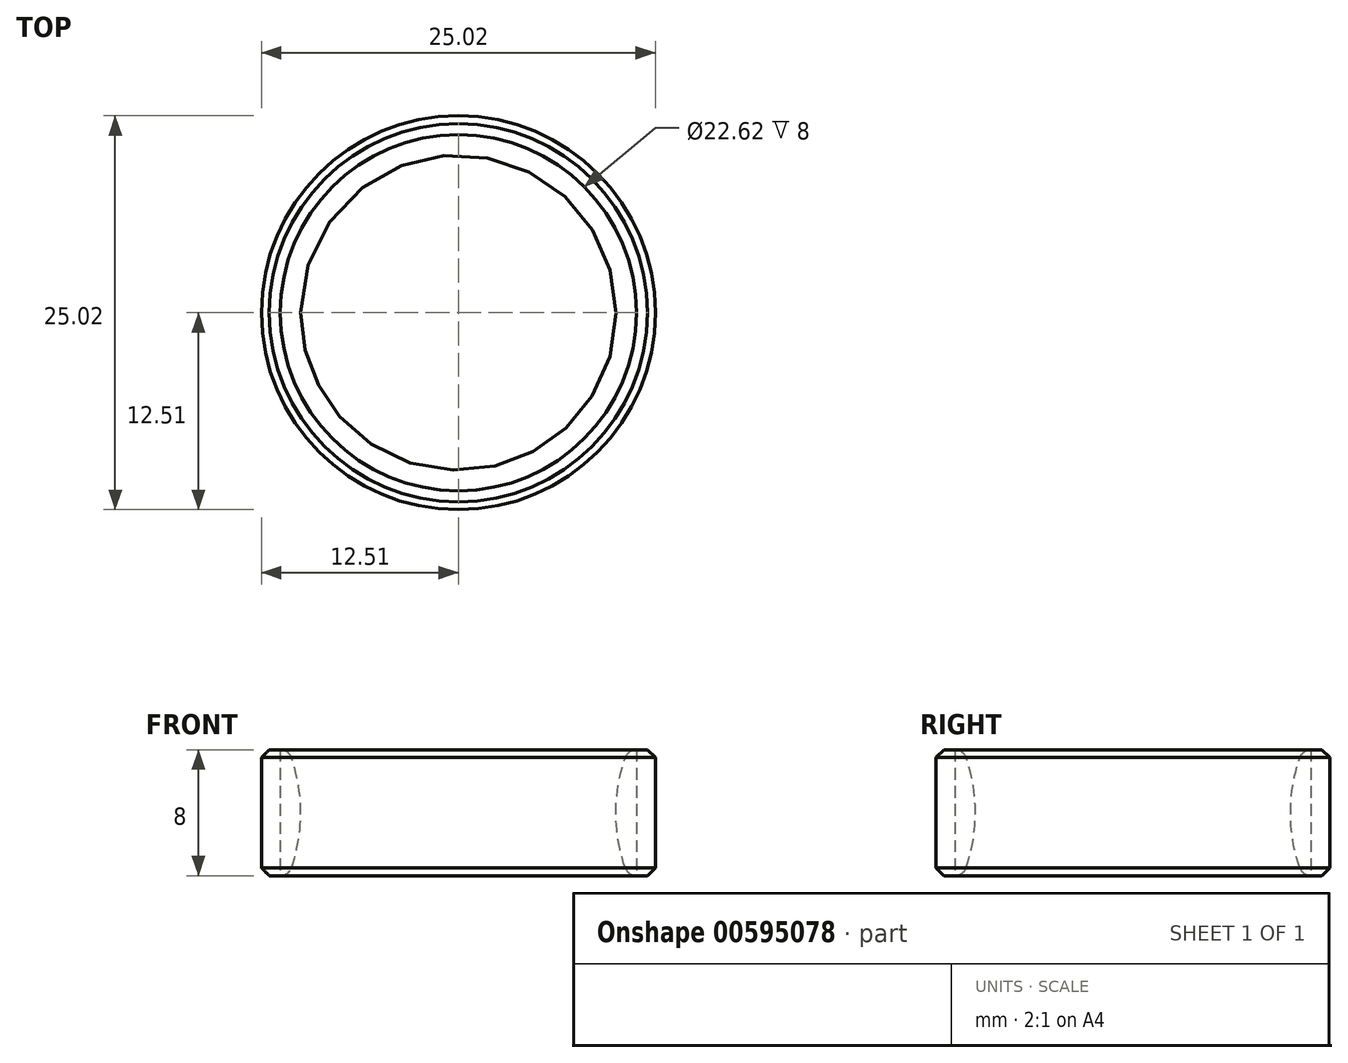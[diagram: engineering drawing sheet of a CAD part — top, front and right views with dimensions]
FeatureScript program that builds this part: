
annotation { "Feature Type Name" : "Feature", "Feature Type Description" : "" }
export const myFeature = defineFeature(function(context is Context, id is Id, definition is map)
    precondition{}
    {
        {
            var Q0;
            Q0=qCreatedBy(makeId("Front.planeOp"),FACE);
            var sketch = newSketch(context, id + "F0", { "sketchPlane" : qUnion([Q0])});
            skLineSegment(sketch, "E0", {"start": v(0, 0) * mm, "end": v(0, 17.87) * mm, "construction": true});
            skArc(sketch, "E1", {"start": v(10.6, 7.5) * mm, "mid": v(10, 4) * mm, "end": v(10.6, 0.5) * mm});
            skLineSegment(sketch, "E2", {"start": v(11.31, 0) * mm, "end": v(12.01, 0) * mm});
            skLineSegment(sketch, "E3", {"start": v(12.01, 0) * mm, "end": v(12.5, 0.5) * mm});
            skLineSegment(sketch, "E4", {"start": v(12.5, 0.5) * mm, "end": v(12.5, 7.5) * mm});
            skLineSegment(sketch, "E5", {"start": v(12.51, 7.5) * mm, "end": v(12.01, 8) * mm});
            skLineSegment(sketch, "E6", {"start": v(12.01, 8) * mm, "end": v(11.3, 8) * mm});
            skLineSegment(sketch, "E7", {"start": v(12.5, 4) * mm, "end": v(20.64, 4) * mm, "construction": true});
            skPoint(sketch, "E8.visualSharp", {"position": v(10.8, 8) * mm});
            skArc(sketch, "E8.filletArc", {"start": v(11.3, 8) * mm, "mid": v(10.88, 7.86) * mm, "end": v(10.6, 7.5) * mm});
            skPoint(sketch, "E9.visualSharp", {"position": v(10.8, 0) * mm});
            skArc(sketch, "E9.filletArc", {"start": v(10.6, 0.5) * mm, "mid": v(10.88, 0.14) * mm, "end": v(11.31, 0) * mm});
            skLineSegment(sketch, "E10", {"start": v(11.31, 8) * mm, "end": v(11.31, 0) * mm});
            skSolve(sketch);
        }
        {
            var Q0;
            Q0=makeQuery(id+"F0.imprint","IMPRINT",FACE,{"disambiguationData":[TD([[makeQuery(id+"F0.imprint","IMPRINT",EDGE,{"derivedFrom":sQuery(id+"F0.wireOp",EDGE,"E1")}),1.0]])]});
            var Q1;
            Q1=sQuery(id+"F0.wireOp",EDGE,"E0");
            revolve(context, id + "F1", {"entities" : qUnion([Q0]), "axis" : qUnion([Q1]), "revolveType" : RevolveType.FULL});
        }
        {
            var Q0;
            Q0=makeQuery(id+"F0.imprint","IMPRINT",FACE,{"disambiguationData":[TD([[makeQuery(id+"F0.imprint","IMPRINT",EDGE,{"derivedFrom":sQuery(id+"F0.wireOp",EDGE,"E2")}),1.0]])]});
            var Q1;
            Q1=sQuery(id+"F0.wireOp",EDGE,"E0");
            revolve(context, id + "F2", {"entities" : qUnion([Q0]), "axis" : qUnion([Q1]), "revolveType" : RevolveType.FULL});
        }
    });
